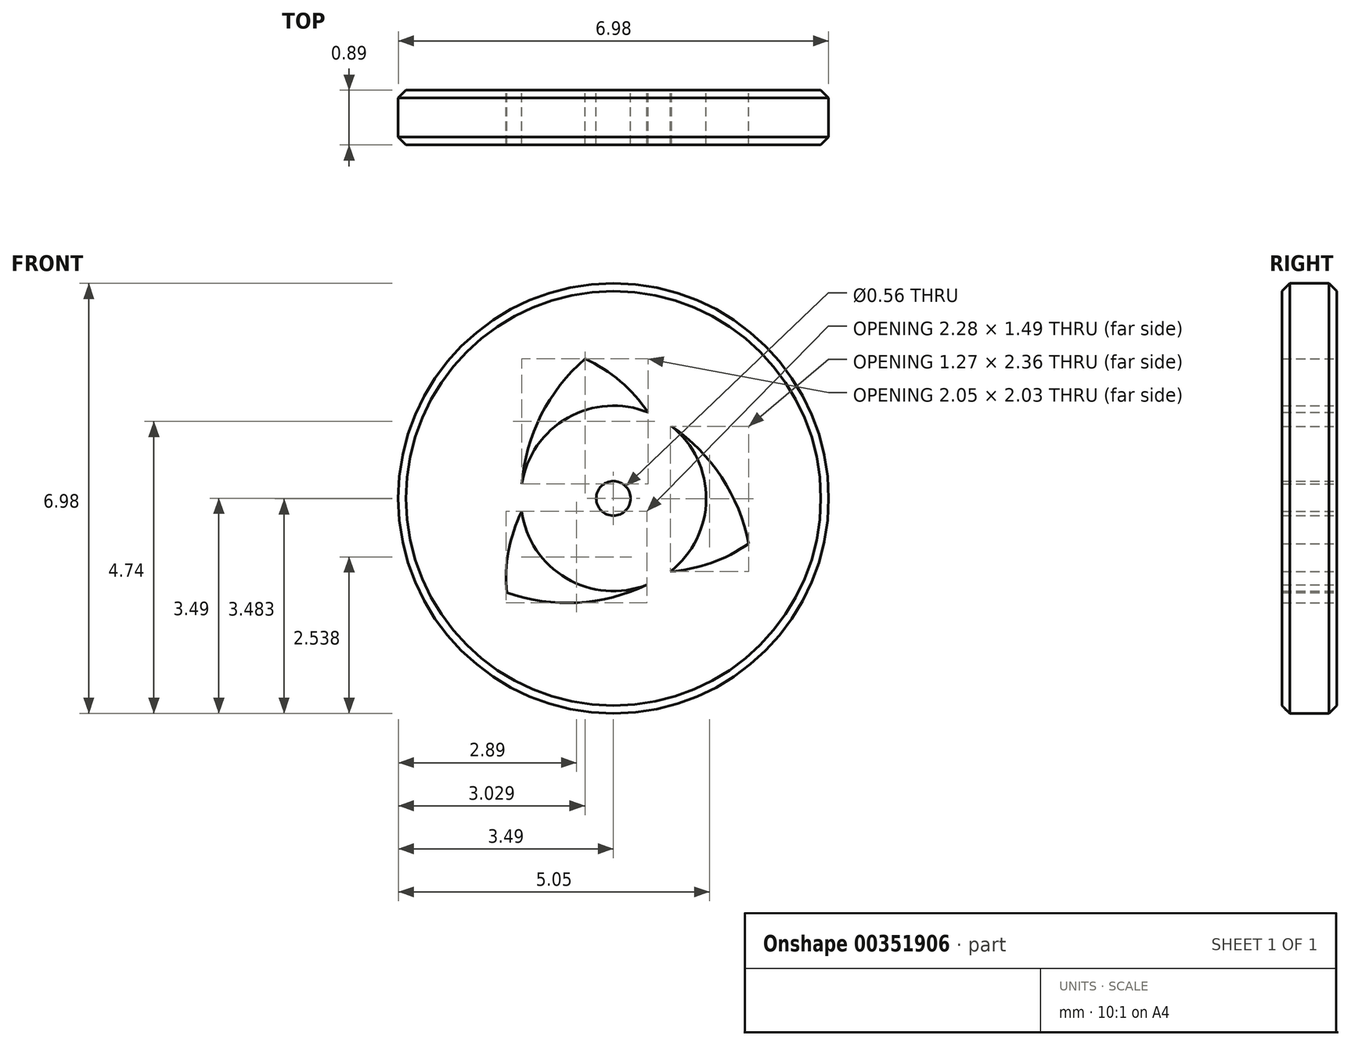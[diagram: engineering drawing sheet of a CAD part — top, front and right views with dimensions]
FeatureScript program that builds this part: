
annotation { "Feature Type Name" : "Feature", "Feature Type Description" : "" }
export const myFeature = defineFeature(function(context is Context, id is Id, definition is map)
    precondition{}
    {
        {
            var Q0;
            Q0=qCreatedBy(makeId("Front.planeOp"),FACE);
            var sketch = newSketch(context, id + "F0", { "sketchPlane" : qUnion([Q0])});
            skCircle(sketch, "E0", {"center": v(0, 0) * mm, "radius": 3.5 * mm});
            skCircle(sketch, "E1", {"center": v(0, 0) * mm, "radius": 0.28 * mm});
            skArc(sketch, "E2", {"start": v(0.56, 1.4) * mm, "mid": v(-0.74, 1.3) * mm, "end": v(-1.49, 0.23) * mm});
            skArc(sketch, "E3", {"start": v(-0.46, 2.27) * mm, "mid": v(-1.17, 1.35) * mm, "end": v(-1.49, 0.23) * mm});
            skArc(sketch, "E4.trimOffspring", {"start": v(0.56, 1.4) * mm, "mid": v(0.11, 1.9) * mm, "end": v(-0.46, 2.27) * mm});
            skArc(sketch, "E5.1.0", {"start": v(-1.73, -1.53) * mm, "mid": v(-0.58, -1.7) * mm, "end": v(0.54, -1.4) * mm});
            skArc(sketch, "E5.1.1", {"start": v(-1.5, -0.2) * mm, "mid": v(-1.7, -0.85) * mm, "end": v(-1.73, -1.53) * mm});
            skArc(sketch, "E5.1.2", {"start": v(-1.5, -0.2) * mm, "mid": v(-0.76, -1.3) * mm, "end": v(0.54, -1.4) * mm});
            skArc(sketch, "E5.2.0", {"start": v(2.2, -0.73) * mm, "mid": v(1.76, 0.34) * mm, "end": v(0.94, 1.17) * mm});
            skArc(sketch, "E5.2.1", {"start": v(0.93, -1.19) * mm, "mid": v(1.6, -1.05) * mm, "end": v(2.2, -0.73) * mm});
            skArc(sketch, "E5.2.2", {"start": v(0.93, -1.19) * mm, "mid": v(1.5, -0.01) * mm, "end": v(0.94, 1.17) * mm});
            skSolve(sketch);
        }
        {
            var Q0;
            Q0 = qSketchRegion(id + "F0", true);
            extrude(context, id + "F1", {"entities" : qUnion([Q0]), "depth" : 0.89 * mm});
        }
        {
            var Q0;
            Q0=makeQuery(id+"F1.opExtrude","CAP_EDGE",EDGE,{"disambiguationData":[OSD([sQuery(id+"F0.wireOp",EDGE,"E0")])],"isStart":false});
            var Q1;
            Q1=makeQuery(id+"F1.opExtrude","CAP_EDGE",EDGE,{"disambiguationData":[OSD([sQuery(id+"F0.wireOp",EDGE,"E0")])],"isStart":true});
            chamfer(context, id + "F2", {"entities" : qUnion([Q0, Q1]), "width" : 0.13 * mm, "tangentPropagation" : true});
        }
    });
